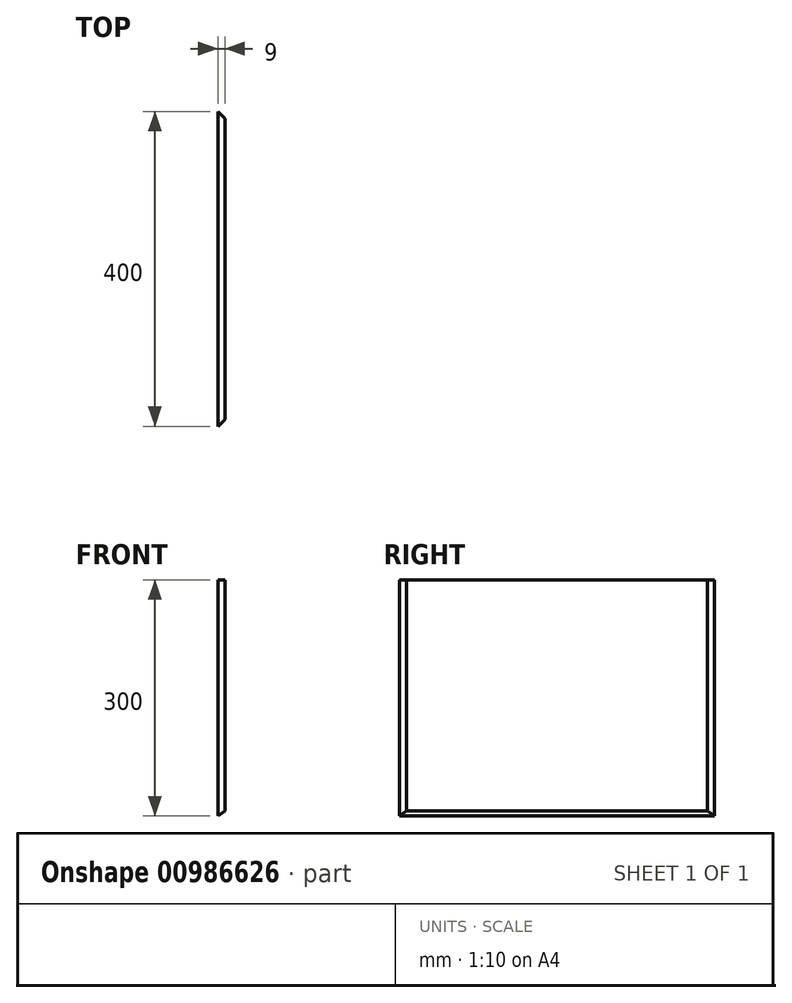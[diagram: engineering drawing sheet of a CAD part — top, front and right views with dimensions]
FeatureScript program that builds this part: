
annotation { "Feature Type Name" : "Feature", "Feature Type Description" : "" }
export const myFeature = defineFeature(function(context is Context, id is Id, definition is map)
    precondition{}
    {
        {
            var Q0;
            Q0=qCreatedBy(makeId("Right.planeOp"),FACE);
            var sketch = newSketch(context, id + "F0", { "sketchPlane" : qUnion([Q0])});
            skLineSegment(sketch, "E0.bottom", {"start": v(-23.8, 286.94) * mm, "end": v(376.2, 286.94) * mm});
            skLineSegment(sketch, "E0.top", {"start": v(-23.8, -13.06) * mm, "end": v(376.2, -13.06) * mm});
            skLineSegment(sketch, "E0.left", {"start": v(-23.8, 286.94) * mm, "end": v(-23.8, -13.06) * mm});
            skLineSegment(sketch, "E0.right", {"start": v(376.2, 286.94) * mm, "end": v(376.2, -13.06) * mm});
            skSolve(sketch);
        }
        {
            var Q0;
            Q0 = qSketchRegion(id + "F0", true);
            var Q1;
            Q1 = qSketchRegion(id + "F4", true);
            extrude(context, id + "F1", {"entities" : qUnion([Q0, Q1]), "depth" : 9 * mm, "offsetDistance" : 25 * mm});
        }
        {
            var Q0;
            Q0=makeQuery(id+"F1.opExtrude","SWEPT_FACE",FACE,{"disambiguationData":[OSD([sQuery(id+"F0.wireOp",EDGE,"E0.bottom")])]});
            var sketch = newSketch(context, id + "F2", { "sketchPlane" : qUnion([Q0])});
            skLineSegment(sketch, "E1", {"start": v(0, 376.2) * mm, "end": v(9, 376.2) * mm});
            skLineSegment(sketch, "E2", {"start": v(9, 376.2) * mm, "end": v(9, 367.2) * mm});
            skLineSegment(sketch, "E3", {"start": v(9, 367.2) * mm, "end": v(0, 376.2) * mm});
            skLineSegment(sketch, "E4", {"start": v(0, -23.8) * mm, "end": v(9, -23.8) * mm});
            skLineSegment(sketch, "E5", {"start": v(9, -14.8) * mm, "end": v(9, -23.8) * mm});
            skLineSegment(sketch, "E6", {"start": v(9, -14.8) * mm, "end": v(0, -23.8) * mm});
            skSolve(sketch);
        }
        {
            var Q0;
            Q0 = qSketchRegion(id + "F2", true);
            extrude(context, id + "F3", {"entities" : qUnion([Q0]), "operationType" : NewBodyOperationType.REMOVE, "oppositeDirection" : true, "depth" : 300 * mm, "offsetDistance" : 25 * mm});
        }
        {
            var Q0;
            Q0=qCreatedBy(makeId("Front.planeOp"),FACE);
            var sketch = newSketch(context, id + "F4", { "sketchPlane" : qUnion([Q0])});
            skLineSegment(sketch, "E7", {"start": v(0, -13.06) * mm, "end": v(9, -13.06) * mm});
            skLineSegment(sketch, "E8", {"start": v(0, -13.06) * mm, "end": v(9, -6.69) * mm});
            skLineSegment(sketch, "E9", {"start": v(9, -6.69) * mm, "end": v(9, -13.06) * mm});
            skSolve(sketch);
        }
        {
            var Q0;
            Q0 = qSketchRegion(id + "F4", true);
            extrude(context, id + "F5", {"entities" : qUnion([Q0]), "operationType" : NewBodyOperationType.REMOVE, "oppositeDirection" : true, "depth" : 400 * mm, "offsetDistance" : 25 * mm});
        }
        {
            var Q0;
            Q0 = qSketchRegion(id + "F4", true);
            extrude(context, id + "F6", {"entities" : qUnion([Q0]), "operationType" : NewBodyOperationType.REMOVE, "depth" : 30 * mm, "offsetDistance" : 25 * mm});
        }
    });
